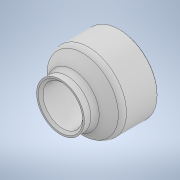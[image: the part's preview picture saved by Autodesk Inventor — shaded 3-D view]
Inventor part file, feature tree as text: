
AUTODESK INVENTOR PART (.ipt)
format: ipt  version: 2021 (Build 250183000, 183)  size: 361,472 bytes
history: native  units: mm
features: fillet x2, sketch x2, revolve x1, plane x1, extrude x1, chamfer x1
ambient origin geometry x8: Origin, YZ Plane, XZ Plane, XY Plane, X Axis, Y Axis, Z Axis, Center Point
bodies: Body1 (feature_tree)
feature tree (8):
  revolve  "Revolution1"  [1 undecoded]
  fillet  "Fillet1"  Radius=37.5mm
  plane  "Work Plane1"
  extrude  "Extrusion2"  Depth=8.0mm
  chamfer  "Chamfer1"  Angle=135.0deg  [1 undecoded]
  fillet  "Fillet2"  Radius=19.5mm
  sketch  "Sketch2"  dims[d4=4.0mm d7=34.0mm d8=37.5mm]
  sketch  "Sketch3"  dims[d9=18.0mm d10=50.0mm d11=135.0deg d15=19.5mm d16=90.0deg d17=8.0mm d18=60.25mm d19=2.0mm d20=0.0mm d21=0.5mm d22=2.0mm d23=45.0deg d24=8.0mm d25=24.0mm d26=45.0deg d27=135.0deg]
note: 2 required parameter values undecoded (feature->parameter linkage not recoverable at this tier; creation-order binding heuristic only, values carry confidence <= 0.55)